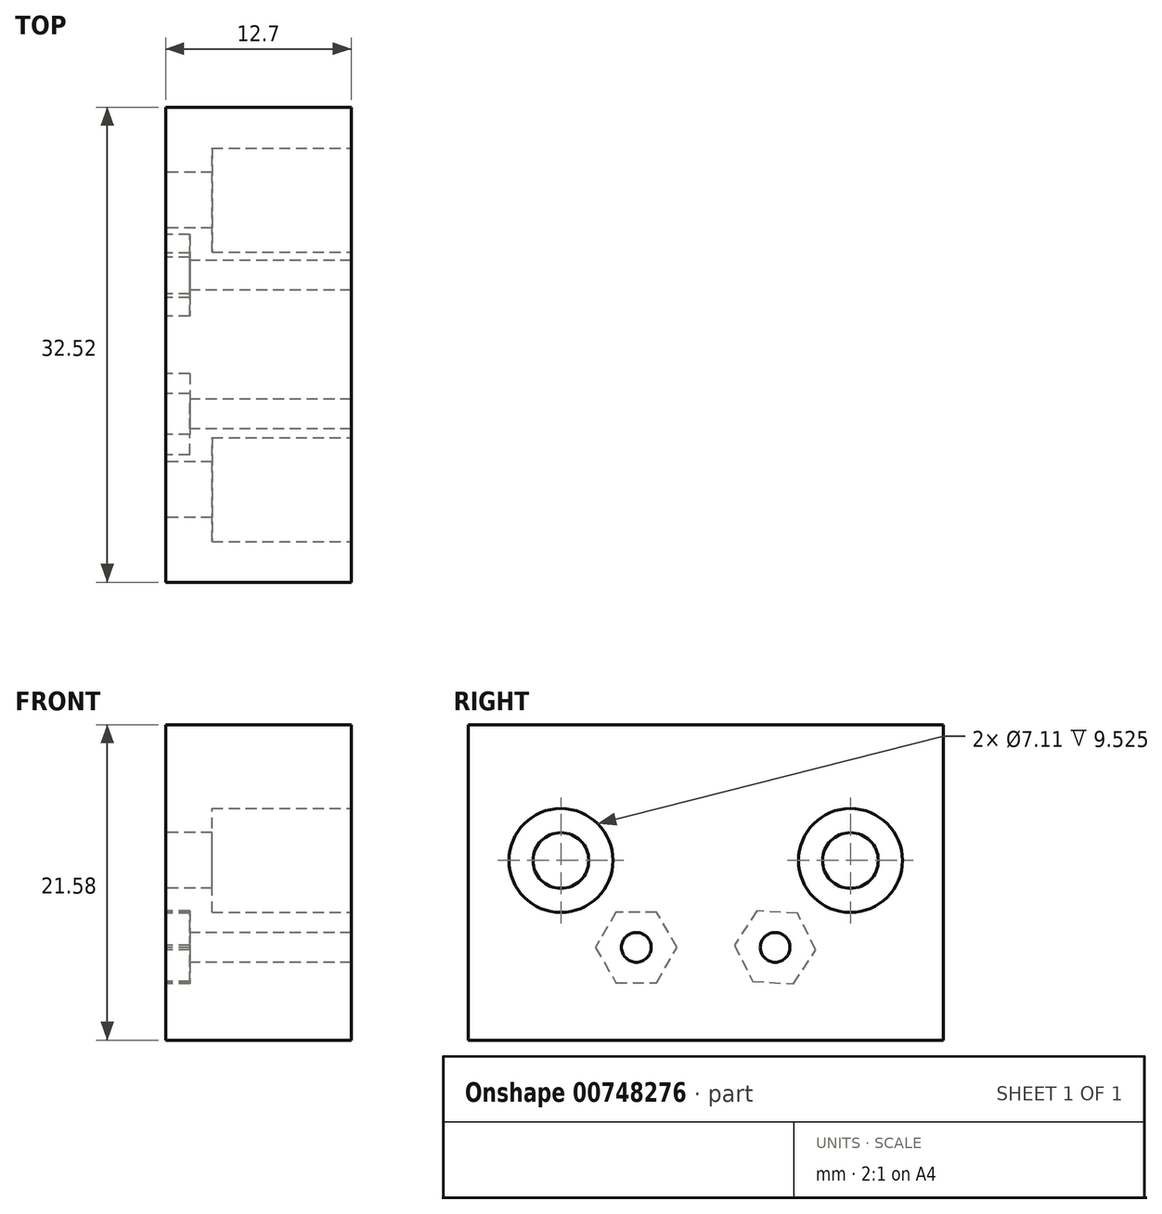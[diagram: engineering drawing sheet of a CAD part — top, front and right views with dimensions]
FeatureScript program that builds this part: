
annotation { "Feature Type Name" : "Feature", "Feature Type Description" : "" }
export const myFeature = defineFeature(function(context is Context, id is Id, definition is map)
    precondition{}
    {
        {
            var Q0;
            Q0=qCreatedBy(makeId("Right.planeOp"),FACE);
            var sketch = newSketch(context, id + "F0", { "sketchPlane" : qUnion([Q0])});
            skLineSegment(sketch, "E0.bottom", {"start": v(9.9, 9.53) * mm, "end": v(-9.9, 9.53) * mm, "construction": true});
            skLineSegment(sketch, "E0.top", {"start": v(9.9, -9.53) * mm, "end": v(-9.9, -9.53) * mm, "construction": true});
            skLineSegment(sketch, "E0.left", {"start": v(9.9, 9.53) * mm, "end": v(9.9, -9.53) * mm, "construction": true});
            skLineSegment(sketch, "E0.right", {"start": v(-9.9, 9.53) * mm, "end": v(-9.9, -9.52) * mm, "construction": true});
            skPoint(sketch, "E0.middle", {"position": v(0, 0) * mm});
            skLineSegment(sketch, "E1", {"start": v(16.26, -3.17) * mm, "end": v(16.26, 18.42) * mm});
            skLineSegment(sketch, "E2", {"start": v(-16.26, -3.17) * mm, "end": v(-16.26, 18.42) * mm});
            skLineSegment(sketch, "E3", {"start": v(-16.26, 18.42) * mm, "end": v(16.26, 18.42) * mm});
            skLineSegment(sketch, "E4", {"start": v(16.26, -3.17) * mm, "end": v(-16.26, -3.17) * mm});
            skSolve(sketch);
        }
        {
            var Q0;
            Q0 = qSketchRegion(id + "F0", true);
            extrude(context, id + "F1", {"entities" : qUnion([Q0]), "depth" : 12.7 * mm, "offsetDistance" : 25.4 * mm});
        }
        {
            var Q0;
            Q0=makeQuery(id+"F1.opExtrude","CAP_FACE",FACE,{"disambiguationData":[OSD([sQuery(id+"F0.wireOp",EDGE,"E1"),sQuery(id+"F0.wireOp",EDGE,"E2"),sQuery(id+"F0.wireOp",EDGE,"E3"),sQuery(id+"F0.wireOp",EDGE,"E4")])],"isStart":true});
            var sketch = newSketch(context, id + "F2", { "sketchPlane" : qUnion([Q0])});
            skLineSegment(sketch, "E5.bottom", {"start": v(4.75, -3.17) * mm, "end": v(-4.75, -3.17) * mm, "construction": true});
            skLineSegment(sketch, "E5.top", {"start": v(4.75, 3.17) * mm, "end": v(-4.75, 3.17) * mm, "construction": true});
            skLineSegment(sketch, "E5.left", {"start": v(4.75, -3.17) * mm, "end": v(4.75, 3.17) * mm, "construction": true});
            skLineSegment(sketch, "E5.right", {"start": v(-4.75, -3.17) * mm, "end": v(-4.75, 3.17) * mm, "construction": true});
            skPoint(sketch, "E5.middle", {"position": v(0, 0) * mm});
            skCircle(sketch, "E6", {"center": v(4.75, 3.17) * mm, "radius": 1.02 * mm});
            skCircle(sketch, "E7", {"center": v(-4.75, 3.17) * mm, "radius": 1.02 * mm});
            skLineSegment(sketch, "E8", {"start": v(-16.26, 9.12) * mm, "end": v(16.26, 9.12) * mm, "construction": true});
            skCircle(sketch, "E9", {"center": v(-9.9, 9.12) * mm, "radius": 1.9 * mm});
            skCircle(sketch, "E10", {"center": v(9.9, 9.12) * mm, "radius": 1.9 * mm});
            skSolve(sketch);
        }
        {
            var Q0;
            Q0 = qSketchRegion(id + "F2", true);
            extrude(context, id + "F3", {"entities" : qUnion([Q0]), "operationType" : NewBodyOperationType.REMOVE, "endBound" : BoundingType.THROUGH_ALL, "oppositeDirection" : true, "depth" : 25.4 * mm, "offsetDistance" : 25.4 * mm});
        }
        {
            var Q0;
            Q0=makeQuery(id+"F1.opExtrude","CAP_FACE",FACE,{"disambiguationData":[OSD([sQuery(id+"F0.wireOp",EDGE,"E1"),sQuery(id+"F0.wireOp",EDGE,"E2"),sQuery(id+"F0.wireOp",EDGE,"E3"),sQuery(id+"F0.wireOp",EDGE,"E4")])],"isStart":true});
            var sketch = newSketch(context, id + "F4", { "sketchPlane" : qUnion([Q0])});
            skCircle(sketch, "E11.cCircle", {"center": v(-4.75, 3.17) * mm, "radius": 2.41 * mm, "construction": true});
            skLineSegment(sketch, "E11.0", {"start": v(-3.5, 5.66) * mm, "end": v(-1.97, 3.33) * mm});
            skLineSegment(sketch, "E11.1", {"start": v(-1.97, 3.33) * mm, "end": v(-3.22, 0.84) * mm});
            skLineSegment(sketch, "E11.2", {"start": v(-3.22, 0.84) * mm, "end": v(-6, 0.69) * mm});
            skLineSegment(sketch, "E11.3", {"start": v(-6, 0.69) * mm, "end": v(-7.53, 3.02) * mm});
            skLineSegment(sketch, "E11.4", {"start": v(-7.53, 3.02) * mm, "end": v(-6.28, 5.5) * mm});
            skLineSegment(sketch, "E11.5", {"start": v(-6.28, 5.5) * mm, "end": v(-3.5, 5.66) * mm});
            skPoint(sketch, "E11.0.midPoint", {"position": v(-2.73, 4.5) * mm});
            skCircle(sketch, "E12.cCircle", {"center": v(4.75, 3.17) * mm, "radius": 2.41 * mm, "construction": true});
            skLineSegment(sketch, "E12.0", {"start": v(3.36, 5.59) * mm, "end": v(6.14, 5.59) * mm});
            skLineSegment(sketch, "E12.1", {"start": v(6.14, 5.59) * mm, "end": v(7.54, 3.17) * mm});
            skLineSegment(sketch, "E12.2", {"start": v(7.54, 3.17) * mm, "end": v(6.14, 0.76) * mm});
            skLineSegment(sketch, "E12.3", {"start": v(6.14, 0.76) * mm, "end": v(3.36, 0.76) * mm});
            skLineSegment(sketch, "E12.4", {"start": v(3.36, 0.76) * mm, "end": v(1.96, 3.18) * mm});
            skLineSegment(sketch, "E12.5", {"start": v(1.96, 3.17) * mm, "end": v(3.36, 5.59) * mm});
            skPoint(sketch, "E12.0.midPoint", {"position": v(4.75, 5.59) * mm});
            skSolve(sketch);
        }
        {
            var Q0;
            Q0 = qSketchRegion(id + "F4", true);
            extrude(context, id + "F5", {"entities" : qUnion([Q0]), "operationType" : NewBodyOperationType.REMOVE, "oppositeDirection" : true, "depth" : 1.65 * mm, "offsetDistance" : 25.4 * mm});
        }
        {
            var Q0;
            Q0=makeQuery(id+"F1.opExtrude","CAP_FACE",FACE,{"disambiguationData":[OSD([sQuery(id+"F0.wireOp",EDGE,"E1"),sQuery(id+"F0.wireOp",EDGE,"E2"),sQuery(id+"F0.wireOp",EDGE,"E3"),sQuery(id+"F0.wireOp",EDGE,"E4")])],"isStart":false});
            var sketch = newSketch(context, id + "F6", { "sketchPlane" : qUnion([Q0])});
            skCircle(sketch, "E13", {"center": v(9.9, 9.12) * mm, "radius": 3.56 * mm});
            skCircle(sketch, "E14", {"center": v(-9.9, 9.12) * mm, "radius": 3.56 * mm});
            skSolve(sketch);
        }
        {
            var Q0;
            Q0 = qSketchRegion(id + "F6", true);
            extrude(context, id + "F7", {"entities" : qUnion([Q0]), "operationType" : NewBodyOperationType.REMOVE, "oppositeDirection" : true, "depth" : 9.52 * mm, "offsetDistance" : 25.4 * mm});
        }
    });
